# Revit family: FA_СтерженьЗаземления_EZETEK
name_source: partatom
category: Системы пожарной сигнализации
revit_build: Autodesk Revit 2017 (Build: 20170118_1100(x64)
units: mm (PartAtom-declared; Revit-internal decimal feet)

## family parameters
Всегда вертикально = Да
На основе рабочей плоскости = Нет
Общий = Нет
При загрузке вырезать с полостями = Нет
Размер круглого соединителя = Использовать радиус
Сохранять ориентацию аннотаций = Нет
Тип детали = Нормальный
Точка расчета площади = Нет

## types (18) — shared parameters
ADSK_Версия Revit = 2017
ADSK_Единица измерения = шт.
ADSK_Завод-изготовитель = Ezetek
ADSK_Количество = 1
URL = https://ezetek.ru
Группа модели = Стержни заземления
Изготовитель = Ezetek
Описание = Стержень заземления представляет собой стальной круглый проводник с резьбой на концах.

## per-type parameters (varying)
| type | ADSK_Код изделия | ADSK_Марка | ADSK_Масса | ADSK_Масса_Текст | ADSK_Материал | ADSK_Наименование | ADSK_Обозначение | ADSK_Размер_Диаметр | ADSK_Размер_Длина | D1 | D2 |
| СтерженьЗаземления_Омедненный_14х1200_90124 | 90124 | 90124 | 1.5 | 1.5 | BIMLIB_Медь_EZETEK | Стержень заземления омедненный 14 мм х 1200 мм | 90124 | 14 мм | 1200 мм | 8 мм | 16 мм |
| СтерженьЗаземления_Омедненный_14х1500_90121 | 90121 | 90121 | 1.9 | 1.9 | BIMLIB_Медь_EZETEK | Стержень заземления омедненный 14 мм х 1500 мм | 90121 | 14 мм | 1500 мм | 8 мм | 16 мм |
| СтерженьЗаземления_Омедненный_16х1500_90125 | 90125 | 90125 | 2.4 | 2.4 | BIMLIB_Медь_EZETEK | Стержень заземления омедненный 16 мм х 1500 мм | 90125 | 16 мм | 1500 мм | 10 мм | 18 мм |
| СтерженьЗаземления_Омедненный_18х1200_61012 | 61012 | 61012 | 3 | 3 | BIMLIB_Медь_EZETEK | Стержень заземления омедненный 18 мм х 1200 мм | 61012 | 18 мм | 1200 мм | 11 мм | 20 мм |
| СтерженьЗаземления_Омедненный_18х1500_61022 | 61022 | 61022 | 3 | 3 | BIMLIB_Медь_EZETEK | Стержень заземления омедненный 18 мм х 1500 мм | 61022 | 18 мм | 1500 мм | 11 мм | 20 мм |
| СтерженьЗаземления_Омедненный_20х1200_61032 | 61032 | 61032 | 3 | 3 | BIMLIB_Медь_EZETEK | Стержень заземления омедненный 20 мм х 1200 мм | 61032 | 20 мм | 1200 мм | 12 мм | 22 мм |
| СтерженьЗаземления_Омедненный_20х1500_61042 | 61042 | 61042 | 3.7 | 3.7 | BIMLIB_Медь_EZETEK | Стержень заземления омедненный 20 мм х 1500 мм | 61042 | 20 мм | 1500 мм | 12 мм | 22 мм |
| СтерженьЗаземления_Оцинкованный_16х1200_90137 | 90137 | 90137 | 1.9 | 1.9 | BIMLIB_Сталь_Оцинкованная_EZETEK | Стержень заземления оцинкованный 16 мм х 1200 мм
Стержень заземления оцинкованный 16 мм х 1200 мм
Стержень заземления оцинкованный 16 мм х 1200 мм | 90137 | 16 мм | 1200 мм | 10 мм | 18 мм |
| СтерженьЗаземления_Оцинкованный_16х1500_90136 | 90136 | 90136 | 2.4 | 2.4 | BIMLIB_Сталь_Оцинкованная_EZETEK | Стержень заземления оцинкованный 16 мм х 1500 мм
Стержень заземления оцинкованный 16 мм х 1200 мм
Стержень заземления оцинкованный 16 мм х 1200 мм | 90136 | 16 мм | 1500 мм | 10 мм | 18 мм |
| СтерженьЗаземления_Оцинкованный_18х1200_61015 | 61015 | 61015 | 2.4 | 2.4 | BIMLIB_Сталь_Оцинкованная_EZETEK | Стержень заземления оцинкованный 18 мм х 1200 мм
Стержень заземления оцинкованный 16 мм х 1200 мм
Стержень заземления оцинкованный 16 мм х 1200 мм | 61015 | 18 мм | 1200 мм | 11 мм | 20 мм |
| СтерженьЗаземления_Оцинкованный_18х1500_61025 | 61025 | 61025 | 3 | 3 | BIMLIB_Сталь_Оцинкованная_EZETEK | Стержень заземления оцинкованный 18 мм х 1500 мм | 61025 | 18 мм | 1500 мм | 11 мм | 20 мм |
| СтерженьЗаземления_Оцинкованный_20х1200_61035 | 61035 | 61035 | 3 | 3 | BIMLIB_Сталь_Оцинкованная_EZETEK | Стержень заземления оцинкованный 20 мм х 1200 мм | 61035 | 20 мм | 1200 мм | 12 мм | 22 мм |
| СтерженьЗаземления_Оцинкованный_20х1500_61045 | 61045 | 61045 | 3.7 | 3.7 | BIMLIB_Сталь_Оцинкованная_EZETEK | Стержень заземления оцинкованный 20 мм х 1500 мм | 61045 | 20 мм | 1500 мм | 12 мм | 22 мм |
| СтерженьЗаземления_ГорЦинкование_16х1500_61064 | 61064 | 61064 | 2.4 | 2.4 | BIMLIB_Сталь_ГорОцинкованная_EZETEK | Стержень заземления оцинкованный 16 мм х 1500 мм, гор.цинк. | 61064 | 16 мм | 1500 мм | 10 мм | 18 мм |
| СтерженьЗаземления_Нержавеющей_16х1500_90133 | 90133 | 90133 | 2.4 | 2.4 | BIMLIB_Сталь_Нержавеющая_EZETEK | Стержень заземления из нержавеющей стали 16 мм х 1500 мм | 90133 | 16 мм | 1500 мм | 10 мм | 18 мм |
| СтерженьЗаземления_Нержавеющей_18х1500_90135 | 90135 | 90135 | 2.4 | 2.4 | BIMLIB_Сталь_Нержавеющая_EZETEK | Стержень заземления из нержавеющей стали 18 мм х 1500 мм
Стержень заземления из нержавеющей стали 18 мм х 1500 мм
Стержень заземления из нержавеющей стали 18 мм х 1500 мм | 90135 | 18 мм | 1500 мм | 11 мм | 20 мм |
| СтерженьЗаземления_Нержавеющей_20х1200_90128 | 90128 | 90128 | 3 | 3 | BIMLIB_Сталь_Нержавеющая_EZETEK | Стержень заземления из нержавеющей стали 20 мм х 1200 мм
Стержень заземления из нержавеющей стали 18 мм х 1500 мм
Стержень заземления из нержавеющей стали 18 мм х 1500 мм | 90128 | 20 мм | 1200 мм | 12 мм | 22 мм |
| СтерженьЗаземления_Нержавеющей_20х1500_90129 | 90129 | 90129 | 3.7 | 3.7 | BIMLIB_Сталь_Нержавеющая_EZETEK | Стержень заземления из нержавеющей стали 20 мм х 1500 мм
Стержень заземления из нержавеющей стали 18 мм х 1500 мм
Стержень заземления из нержавеющей стали 18 мм х 1500 мм | 90129 | 20 мм | 1500 мм | 12 мм | 22 мм |
